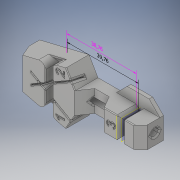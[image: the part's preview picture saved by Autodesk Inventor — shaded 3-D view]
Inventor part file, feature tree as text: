
AUTODESK INVENTOR PART (.ipt)
format: ipt  version: 2019.4 (Build 234330000, 330)  size: 2,168,320 bytes
history: native  units: in
note: dims shown in document units (in); Inventor stores cm internally (conversion verified against a paired STEP export)
features: extrude x5, sketch x5, other x3, plane x2, fillet x2, chamfer x2, projected_geometry x2
ambient origin geometry x8: Origin, YZ Plane, XZ Plane, XY Plane, X Axis, Y Axis, Z Axis, Center Point
bodies: Solid1 (feature_tree), Body3 (feature_tree)
feature tree (21):
  other  "Annotations"
  plane  "Work Plane1"
  extrude  "Extrusion1"  Depth=0.0394in TaperAngle=0.0deg
  plane  "Work Plane2"
  extrude  "Extrusion2"  Depth=0.0787in TaperAngle=0.0deg
  extrude  "Extrusion3"  Depth=0.0197in
  fillet  "Fillet1"  Radius=0.0197in
  chamfer  "Chamfer1"  Distance=0.0394in
  chamfer  "Chamfer2"  Distance=0.0236in
  fillet  "Fillet2"  [1 undecoded]
  extrude  "Extrusion4"  [1 undecoded]
  extrude  "Extrusion5"  [1 undecoded]
  sketch  "Sketch1"  dims[d3=-0.0394in d4=0.0394in d5=0.0in]
  sketch  "Sketch2"  dims[d6=-0.0394in d7=0.0787in d8=0.0in]
  sketch  "Sketch3"  dims[d9=0.0787in d10=0.0in d11=0.0197in]
  sketch  "Sketch4"  dims[d12=0.0787in d13=0.0787in d14=45.0deg]
  sketch  "Sketch5"  dims[d15=0.0787in d16=0.0787in d17=45.0deg d18=0.0197in d19=0.0394in d20=0.0in d21=0.0236in d22=0.0in d0=0.2309in d1=0.1141in d2=1.526in d23=0.2012in d24=0.0906in d25=1.5654in]
  projected_geometry  "Project Cut Edges1"
  projected_geometry  "Project Cut Edges2"
  other  "Linear Dimension 1"
  other  "Linear Dimension 2"
note: 3 required parameter values undecoded (feature->parameter linkage not recoverable at this tier; creation-order binding heuristic only, values carry confidence <= 0.55)
